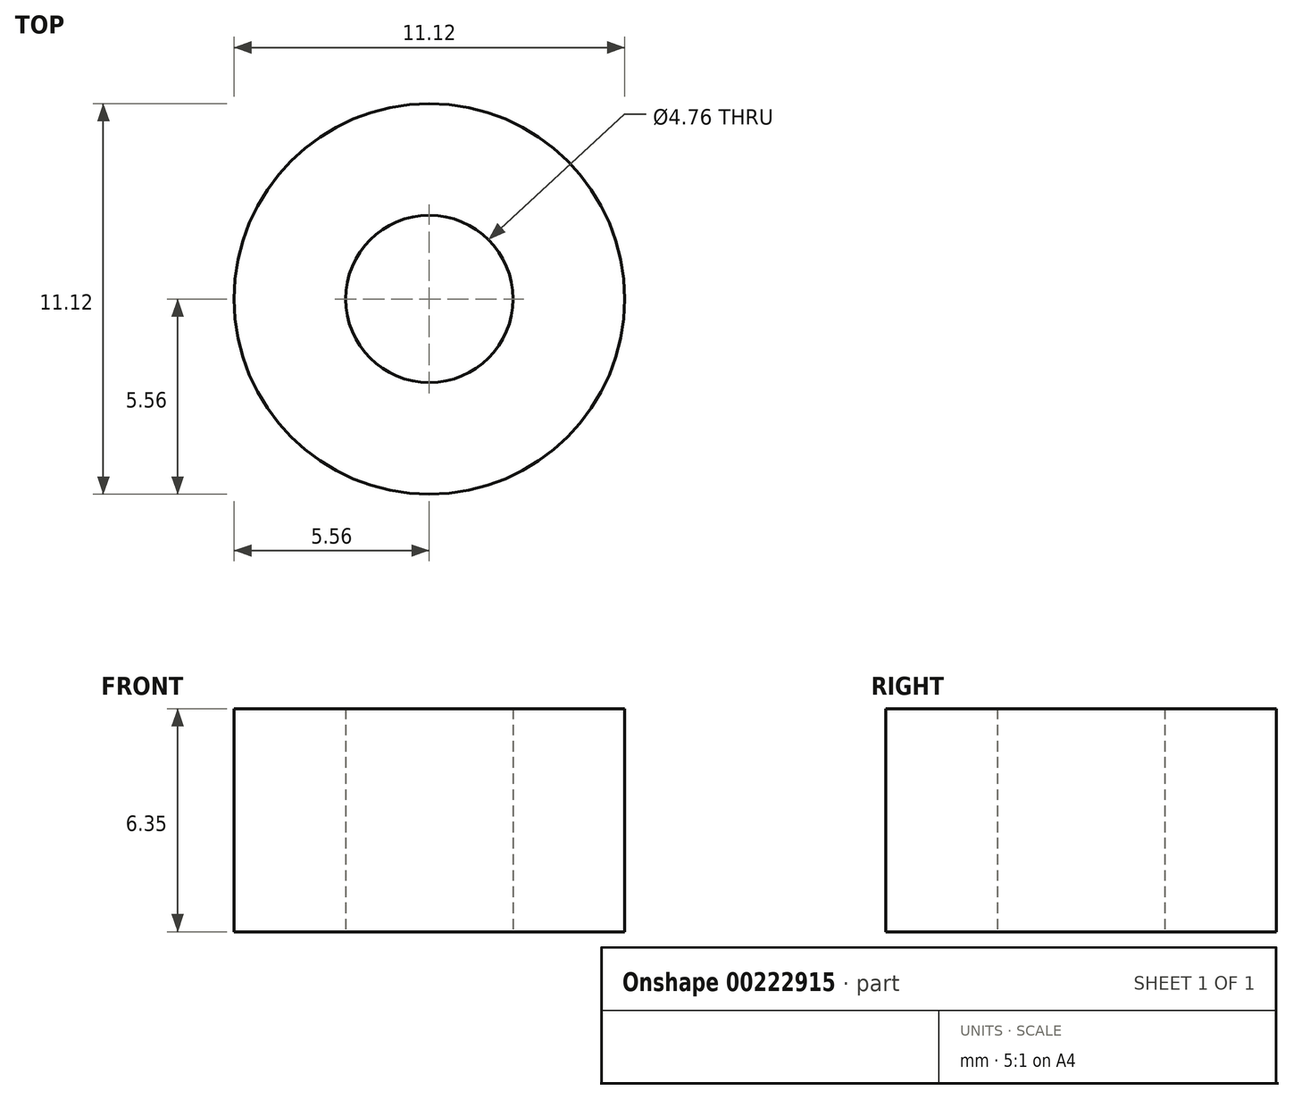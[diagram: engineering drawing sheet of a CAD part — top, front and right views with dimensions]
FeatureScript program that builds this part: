
annotation { "Feature Type Name" : "Feature", "Feature Type Description" : "" }
export const myFeature = defineFeature(function(context is Context, id is Id, definition is map)
    precondition{}
    {
        {
            var Q0;
            Q0=qCreatedBy(makeId("Top.planeOp"),FACE);
            var sketch = newSketch(context, id + "F0", { "sketchPlane" : qUnion([Q0])});
            skCircle(sketch, "E0", {"center": v(0, 0) * mm, "radius": 5.56 * mm});
            skCircle(sketch, "E1", {"center": v(0, 0) * mm, "radius": 2.38 * mm});
            skSolve(sketch);
        }
        {
            var Q0;
            Q0=makeQuery(id+"F0.imprint","IMPRINT",FACE,{"disambiguationData":[TD([[makeQuery(id+"F0.imprint","IMPRINT",EDGE,{"derivedFrom":sQuery(id+"F0.wireOp",EDGE,"E0")}),1.0]])]});
            extrude(context, id + "F1", {"entities" : qUnion([Q0]), "depth" : 6.35 * mm});
        }
    });
